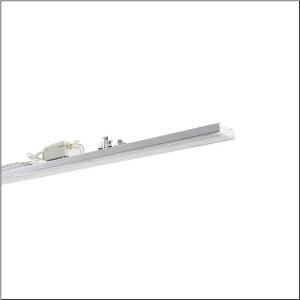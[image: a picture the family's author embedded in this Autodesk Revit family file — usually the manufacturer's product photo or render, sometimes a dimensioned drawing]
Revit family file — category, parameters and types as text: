
# Revit family: licross_11_recessed_mo_51tl127n485g
name_source: partatom
category: Lighting Fixtures
units: mm (PartAtom-declared; Revit-internal decimal feet)

## family parameters
Cut with Voids When Loaded = No
Host = Face
Light Source = No
Part Type = Normal
Room Calculation Point = No
Round Connector Dimension = Use Diameter
Shared = No

## types (1)
- Licross 11 Recessed MO (1 x LED, 8950 lm, 48.5 W, 4000K)
    Apparent Load = 49 VA
    CIE Flux Codes = 67 92 99 100 100
    Color Rendering = 80
    Color Temperature = 4000K
    Default Elevation = 1800 mm
    Description = Licross 11 Recessed MO, luminaire insert, of sheet steel, coil coated, white, length: 1.500mm, width: 66mm, height: 67mm, LED rated luminous flux: 8.950lm, light colour: 840, SDCM (Standard Deviation of Colour Matching)MacAdam ≤ 2 SDCM (initial), control gear: ON/OFF, with plug, 3-pole, with phase selection, mains connection: 220..240V, AC, 50/60Hz, rated input power: 49W, internal wiring halogen-free, primary optical cover: cover, of PMMA, light emission: direct distribution, primary light characteristic: symmetric, protection rating (complete): IP40, insulation class (complete): insulation class I (protective earthing), certification: CE, ENEC, VDE, UKCA, protection symbol: D if used in an environment without relevant dust loads with corresponding accessories, impact resistance: IK06, permissible ambient temperature for indoor applications: -35..+35°C, corresponds to IFS (International Featured Standards) requirements for safety and quality in the food industry, reducing of maximum allowable ambient temperature of 5°C with ceiling mounting, The light source and the operating device comply with the requirements of the Ecodesign Regulation (EU) 2019/2020 and are replaceable in accordance with this regulation, packaging unit: 1 piece
    Height = 58 mm
    Lamp = 1 x LED
    Lamp Light Flux = 8950 lm
    Lamp Power = 48.5 W
    Lamp count = 1
    Length = 1500 mm
    Luminous efficacy = 185 lm/W
    Manufacturer = Siteco
    ModVariant = No
    Model = 51TL127N485G
    Mounting Place = Ceiling
    Mounting Type = Pendant
    Number of Poles = 1
    OnlyDefault = Yes
    Power Factor = 1
    Product Name = Licross 11 Recessed MO
    Product group = luminaire insert | ceiling pendant
    ProductGroupID = 901
    Protection Class = Protection class I
    Protection Degree = IP 40
    RLX_Detail_Level = 1
    RLX_Emergency_Light_Flux = 0 lm
    RLX_Emergency_Type = 0
    RLX_Emergency_Type_DB = No
    RlxData = <blob elided: 20989 chars, md5=4d144f26>
    Socket = socket
    Standby Power = 0 W
    System Light Flux = 8950 lm
    System Power = 49 W
    Type Comments = Product without accessories
    Type Image = l_1296930.jpg
    URL = http://relux.com
    VarID = ---
    Voltage = 0 V
    Weight = 0.00 kg
    Width = 66 mm

## geometry (parser evidence)
native form markers: Blend x4, Sweep x10
no freeform markers — native parametric forms only
